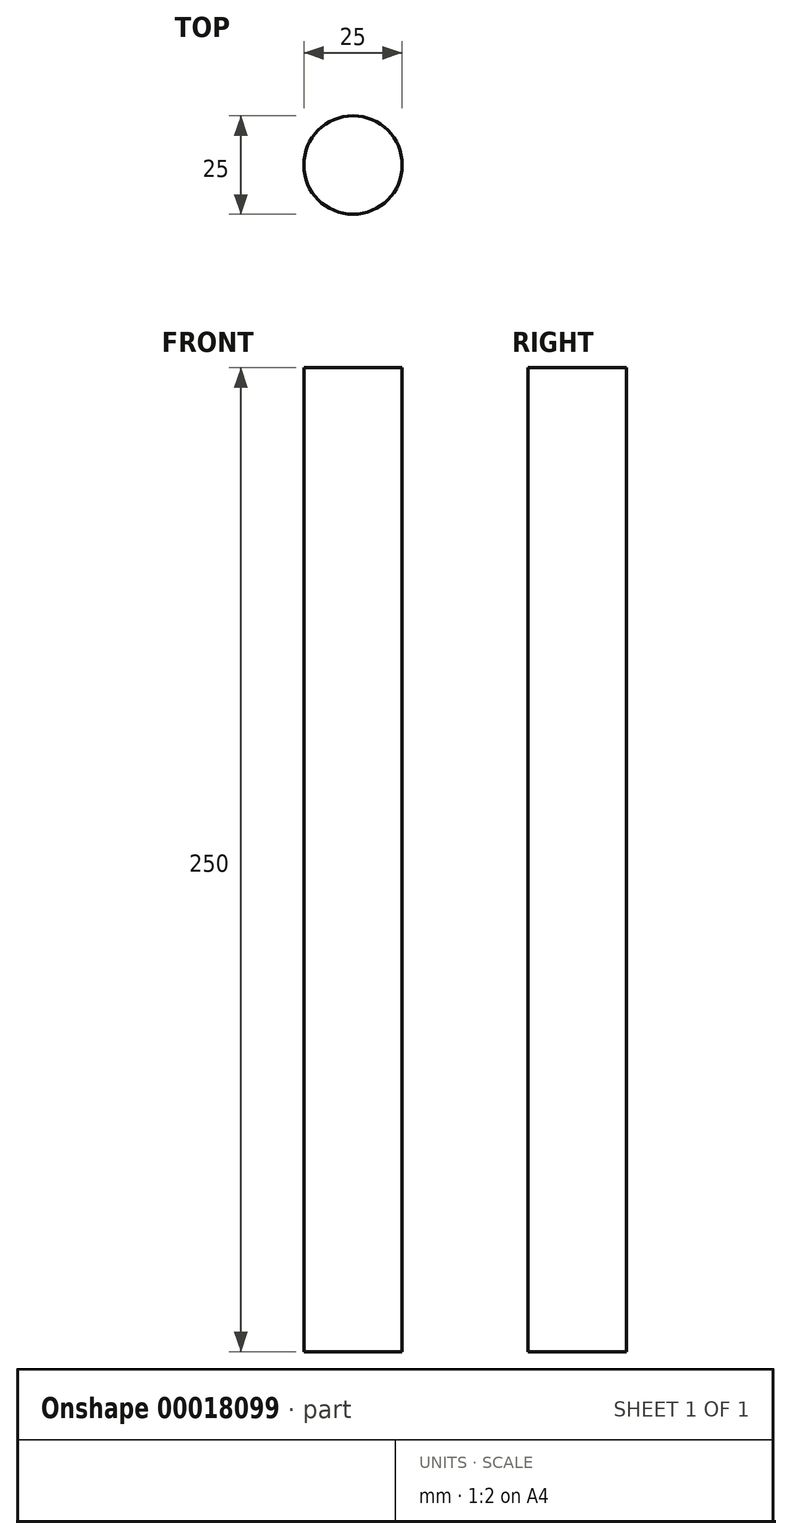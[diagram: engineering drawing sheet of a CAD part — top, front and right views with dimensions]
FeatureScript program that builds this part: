
annotation { "Feature Type Name" : "Feature", "Feature Type Description" : "" }
export const myFeature = defineFeature(function(context is Context, id is Id, definition is map)
    precondition{}
    {
        {
            var Q0;
            Q0=qCreatedBy(makeId("Top.planeOp"),FACE);
            var sketch = newSketch(context, id + "F0", { "sketchPlane" : qUnion([Q0])});
            skCircle(sketch, "E0", {"center": v(0, 0) * mm, "radius": 12.5 * mm});
            skSolve(sketch);
        }
        {
            var Q0;
            Q0 = qSketchRegion(id + "F0", true);
            extrude(context, id + "F1", {"entities" : qUnion([Q0]), "depth" : 250 * mm});
        }
    });
